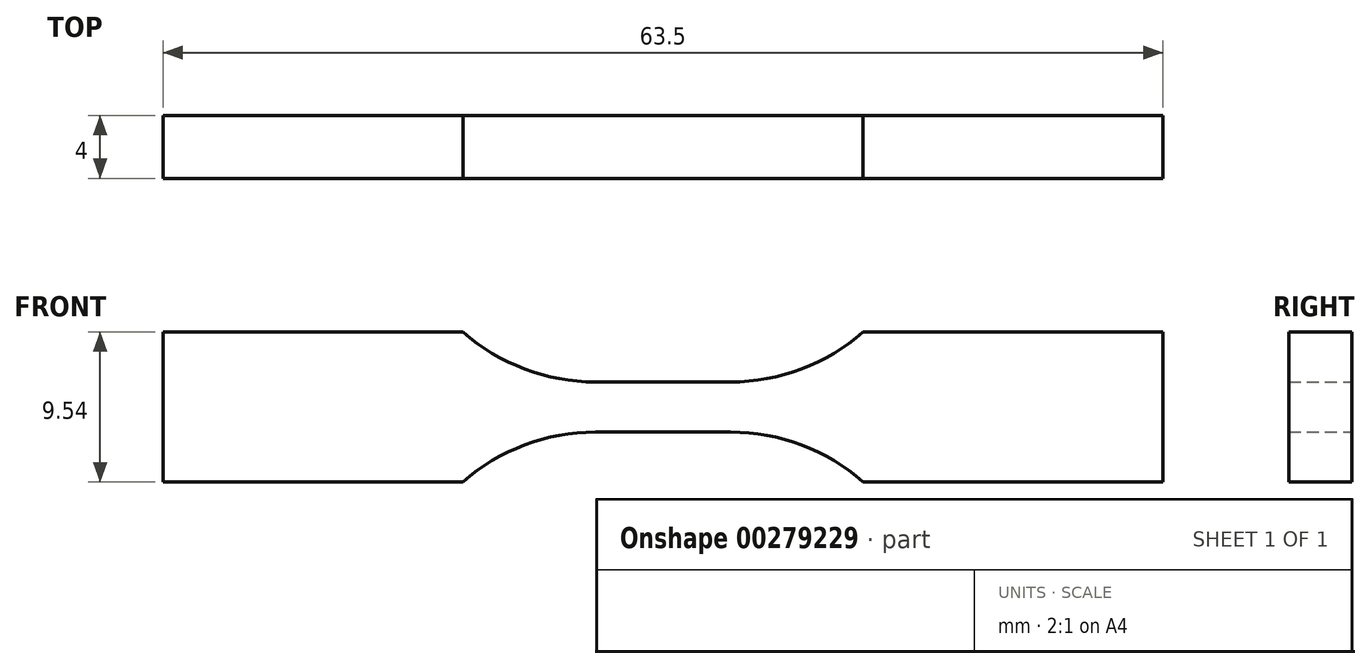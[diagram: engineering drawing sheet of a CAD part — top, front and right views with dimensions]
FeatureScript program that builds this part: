
annotation { "Feature Type Name" : "Feature", "Feature Type Description" : "" }
export const myFeature = defineFeature(function(context is Context, id is Id, definition is map)
    precondition{}
    {
        {
            var Q0;
            Q0=qCreatedBy(makeId("Front.planeOp"),FACE);
            var sketch = newSketch(context, id + "F0", { "sketchPlane" : qUnion([Q0])});
            skLineSegment(sketch, "E0", {"start": v(0, 1.6) * mm, "end": v(4.3, 1.6) * mm});
            skArc(sketch, "E1", {"start": v(4.3, 1.6) * mm, "mid": v(8.79, 2.41) * mm, "end": v(12.7, 4.76) * mm});
            skLineSegment(sketch, "E2", {"start": v(12.7, 4.77) * mm, "end": v(31.75, 4.77) * mm});
            skLineSegment(sketch, "E3.MirrorCS", {"start": v(0, -1.6) * mm, "end": v(4.3, -1.6) * mm});
            skLineSegment(sketch, "E4.MirrorCS", {"start": v(12.7, -4.76) * mm, "end": v(31.75, -4.76) * mm});
            skArc(sketch, "E5.MirrorCS", {"start": v(4.3, -1.6) * mm, "mid": v(8.79, -2.41) * mm, "end": v(12.7, -4.76) * mm});
            skArc(sketch, "E6.MirrorCS", {"start": v(-4.3, 1.6) * mm, "mid": v(-8.79, 2.41) * mm, "end": v(-12.7, 4.76) * mm});
            skArc(sketch, "E7.MirrorCS", {"start": v(-4.3, -1.6) * mm, "mid": v(-8.79, -2.41) * mm, "end": v(-12.7, -4.76) * mm});
            skLineSegment(sketch, "E8.MirrorCS", {"start": v(0, 1.6) * mm, "end": v(-4.3, 1.6) * mm});
            skLineSegment(sketch, "E9.MirrorCS", {"start": v(-12.7, 4.76) * mm, "end": v(-31.75, 4.76) * mm});
            skLineSegment(sketch, "E10.MirrorCS", {"start": v(0, -1.59) * mm, "end": v(-4.3, -1.59) * mm});
            skLineSegment(sketch, "E11.MirrorCS", {"start": v(-12.7, -4.77) * mm, "end": v(-31.75, -4.77) * mm});
            skLineSegment(sketch, "E12", {"start": v(-31.75, -4.77) * mm, "end": v(-31.75, 4.77) * mm});
            skLineSegment(sketch, "E13", {"start": v(31.75, -4.77) * mm, "end": v(31.75, 4.77) * mm});
            skSolve(sketch);
        }
        {
            var Q0;
            Q0 = qSketchRegion(id + "F0", true);
            extrude(context, id + "F1", {"entities" : qUnion([Q0]), "endBound" : BoundingType.SYMMETRIC, "depth" : 4 * mm});
        }
    });
